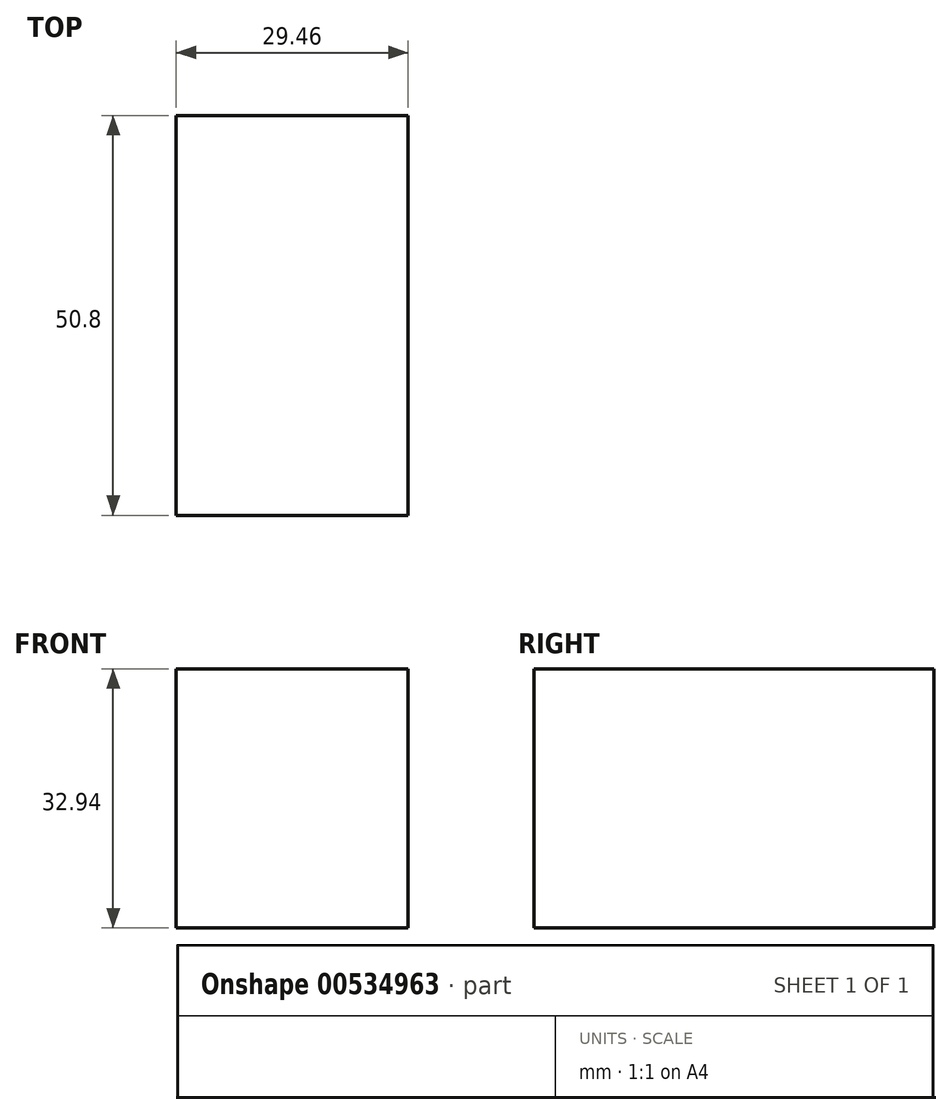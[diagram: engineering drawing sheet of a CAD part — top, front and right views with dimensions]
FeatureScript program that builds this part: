
annotation { "Feature Type Name" : "Feature", "Feature Type Description" : "" }
export const myFeature = defineFeature(function(context is Context, id is Id, definition is map)
    precondition{}
    {
        {
            var Q0;
            Q0=qCreatedBy(makeId("Front.planeOp"),FACE);
            var sketch = newSketch(context, id + "F0", { "sketchPlane" : qUnion([Q0])});
            skLineSegment(sketch, "E0.bottom", {"start": v(0, 0) * mm, "end": v(29.46, 0) * mm});
            skLineSegment(sketch, "E0.top", {"start": v(0, -32.94) * mm, "end": v(29.46, -32.94) * mm});
            skLineSegment(sketch, "E0.left", {"start": v(0, 0) * mm, "end": v(0, -32.94) * mm});
            skLineSegment(sketch, "E0.right", {"start": v(29.46, 0) * mm, "end": v(29.46, -32.94) * mm});
            skSolve(sketch);
        }
        {
            var Q0;
            Q0=makeQuery(id+"F0.imprint","IMPRINT",FACE,{"disambiguationData":[TD([[makeQuery(id+"F0.imprint","IMPRINT",EDGE,{"derivedFrom":sQuery(id+"F0.wireOp",EDGE,"E0.bottom")}),-1.0]])]});
            extrude(context, id + "F1", {"entities" : qUnion([Q0]), "depth" : 25.4 * mm, "offsetDistance" : 25.4 * mm, "hasSecondDirection" : true, "secondDirectionOppositeDirection" : true, "secondDirectionDepth" : 25.4 * mm});
        }
    });
